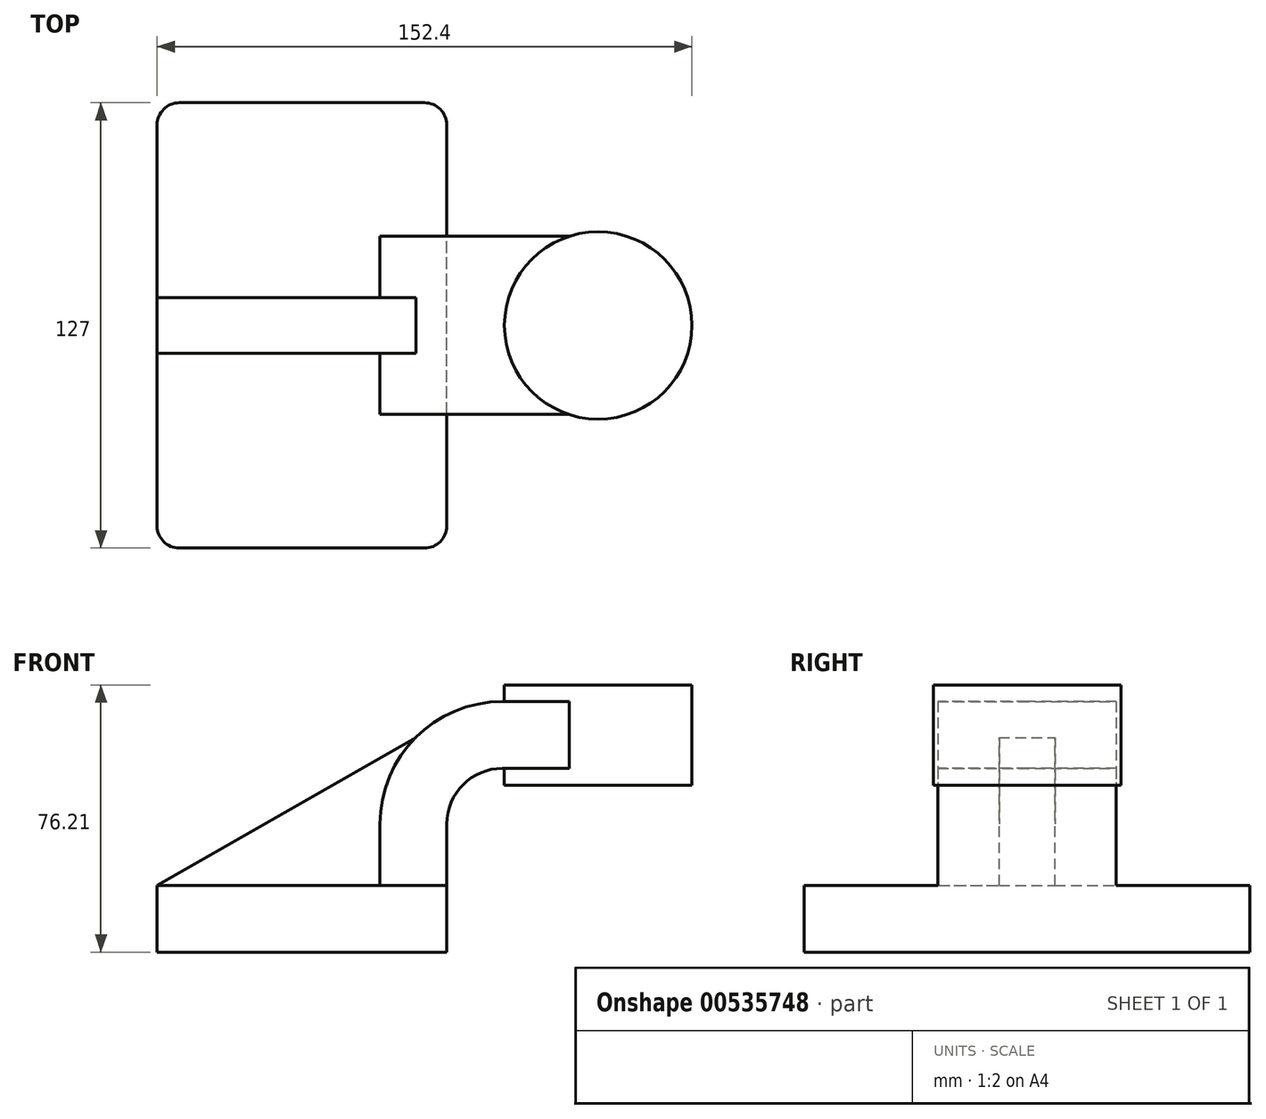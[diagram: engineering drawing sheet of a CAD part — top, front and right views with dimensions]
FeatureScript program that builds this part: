
annotation { "Feature Type Name" : "Feature", "Feature Type Description" : "" }
export const myFeature = defineFeature(function(context is Context, id is Id, definition is map)
    precondition{}
    {
        {
            var Q0;
            Q0=qCreatedBy(makeId("Front.planeOp"),FACE);
            var sketch = newSketch(context, id + "F0", { "sketchPlane" : qUnion([Q0])});
            skLineSegment(sketch, "E0.bottom", {"start": v(41.27, 9.53) * mm, "end": v(-41.28, 9.53) * mm});
            skLineSegment(sketch, "E0.top", {"start": v(41.28, -9.52) * mm, "end": v(-41.27, -9.52) * mm});
            skLineSegment(sketch, "E0.left", {"start": v(41.28, 9.53) * mm, "end": v(41.28, -9.52) * mm});
            skLineSegment(sketch, "E0.right", {"start": v(-41.28, 9.53) * mm, "end": v(-41.27, -9.52) * mm});
            skPoint(sketch, "E0.middle", {"position": v(0, 0) * mm});
            skLineSegment(sketch, "E1.bottom", {"start": v(111.13, 66.68) * mm, "end": v(60.33, 66.68) * mm});
            skLineSegment(sketch, "E1.top", {"start": v(111.12, 38.1) * mm, "end": v(60.33, 38.1) * mm});
            skLineSegment(sketch, "E1.left", {"start": v(111.13, 66.68) * mm, "end": v(111.13, 38.1) * mm});
            skLineSegment(sketch, "E1.right", {"start": v(60.33, 66.68) * mm, "end": v(60.33, 38.1) * mm});
            skPoint(sketch, "E1.middle", {"position": v(85.72, 52.39) * mm});
            skLineSegment(sketch, "E2", {"start": v(41.27, 9.53) * mm, "end": v(41.27, 27) * mm});
            skArc(sketch, "E3", {"start": v(41.27, 27) * mm, "mid": v(45.92, 38.23) * mm, "end": v(57.15, 42.88) * mm});
            skLineSegment(sketch, "E4", {"start": v(57.15, 42.88) * mm, "end": v(101.82, 42.88) * mm});
            skLineSegment(sketch, "E5.0", {"start": v(57.15, 61.93) * mm, "end": v(84.4, 61.93) * mm});
            skArc(sketch, "E5.1", {"start": v(22.23, 27) * mm, "mid": v(32.45, 51.7) * mm, "end": v(57.15, 61.93) * mm});
            skLineSegment(sketch, "E5.2", {"start": v(22.22, 7.79) * mm, "end": v(22.22, 27) * mm});
            skLineSegment(sketch, "E6", {"start": v(84.4, 38.1) * mm, "end": v(84.4, 66.68) * mm});
            skLineSegment(sketch, "E7", {"start": v(-41.28, 9.52) * mm, "end": v(32.45, 51.7) * mm});
            skSolve(sketch);
        }
        {
            var Q0;
            Q0=makeQuery(id+"F0.imprint","IMPRINT",FACE,{"disambiguationData":[TD([[makeQuery(id+"F0.imprint","IMPRINT",EDGE,{"derivedFrom":sQuery(id+"F0.wireOp",EDGE,"E0.top")}),-1.0]])]});
            extrude(context, id + "F1", {"entities" : qUnion([Q0]), "endBound" : BoundingType.SYMMETRIC, "depth" : 127 * mm, "offsetDistance" : 25.4 * mm});
        }
        {
            var Q0;
            {var subQ0=sQuery(id+"F0.wireOp",EDGE,"E5.0");var subQ1=sQuery(id+"F0.wireOp",EDGE,"E1.right");var subQ2=makeQuery(id+"F0.imprint","INTERSECT",VERTEX,{"derivedFrom":[subQ1,subQ0]});Q0=makeQuery(id+"F0.imprint","IMPRINT",FACE,{"disambiguationData":[TD([[makeQuery(id+"F0.imprint","IMPRINT",EDGE,{"disambiguationData":[TD([[subQ2,-1.0]])],"derivedFrom":subQ1}),1.0]])]});}
            var Q1;
            {var subQ1=sQuery(id+"F0.wireOp",EDGE,"E2");Q1=makeQuery(id+"F0.imprint","IMPRINT",FACE,{"disambiguationData":[TD([[makeQuery(id+"F0.imprint","IMPRINT",EDGE,{"derivedFrom":subQ1}),1.0]])]});}
            extrude(context, id + "F2", {"entities" : qUnion([Q0, Q1]), "operationType" : NewBodyOperationType.ADD, "endBound" : BoundingType.SYMMETRIC, "depth" : 50.8 * mm, "offsetDistance" : 25.4 * mm});
        }
        {
            var Q0;
            {var subQ0=sQuery(id+"F0.wireOp",EDGE,"E7");Q0=makeQuery(id+"F0.imprint","IMPRINT",FACE,{"disambiguationData":[TD([[makeQuery(id+"F0.imprint","IMPRINT",EDGE,{"derivedFrom":subQ0}),-1.0]])]});}
            extrude(context, id + "F3", {"entities" : qUnion([Q0]), "operationType" : NewBodyOperationType.ADD, "endBound" : BoundingType.SYMMETRIC, "depth" : 15.88 * mm, "offsetDistance" : 25.4 * mm});
        }
        {
            var Q0;
            {var subQ0=sQuery(id+"F0.wireOp",EDGE,"E1.left");Q0=makeQuery(id+"F0.imprint","IMPRINT",FACE,{"disambiguationData":[TD([[makeQuery(id+"F0.imprint","IMPRINT",EDGE,{"derivedFrom":subQ0}),-1.0]])]});}
            var Q1;
            Q1=sQuery(id+"F0.wireOp",EDGE,"E6");
            revolve(context, id + "F4", {"operationType" : NewBodyOperationType.ADD, "entities" : qUnion([Q0]), "axis" : qUnion([Q1]), "revolveType" : RevolveType.FULL});
        }
        {
            var Q0;
            Q0=makeQuery(id+"F1.opExtrude","CAP_EDGE",EDGE,{"disambiguationData":[OSD([sQuery(id+"F0.wireOp",EDGE,"E0.left")])],"isStart":false});
            var Q1;
            Q1=makeQuery(id+"F1.opExtrude","CAP_EDGE",EDGE,{"disambiguationData":[OSD([sQuery(id+"F0.wireOp",EDGE,"E0.right")])],"isStart":false});
            var Q2;
            Q2=makeQuery(id+"F1.opExtrude","CAP_EDGE",EDGE,{"disambiguationData":[OSD([sQuery(id+"F0.wireOp",EDGE,"E0.right")])],"isStart":true});
            var Q3;
            Q3=makeQuery(id+"F1.opExtrude","CAP_EDGE",EDGE,{"disambiguationData":[OSD([sQuery(id+"F0.wireOp",EDGE,"E0.left")])],"isStart":true});
            fillet(context, id + "F5", {"entities" : qUnion([Q0, Q1, Q2, Q3]), "radius" : 6.35 * mm, "tangentPropagation" : true, "allowEdgeOverflow" : false});
        }
    });
